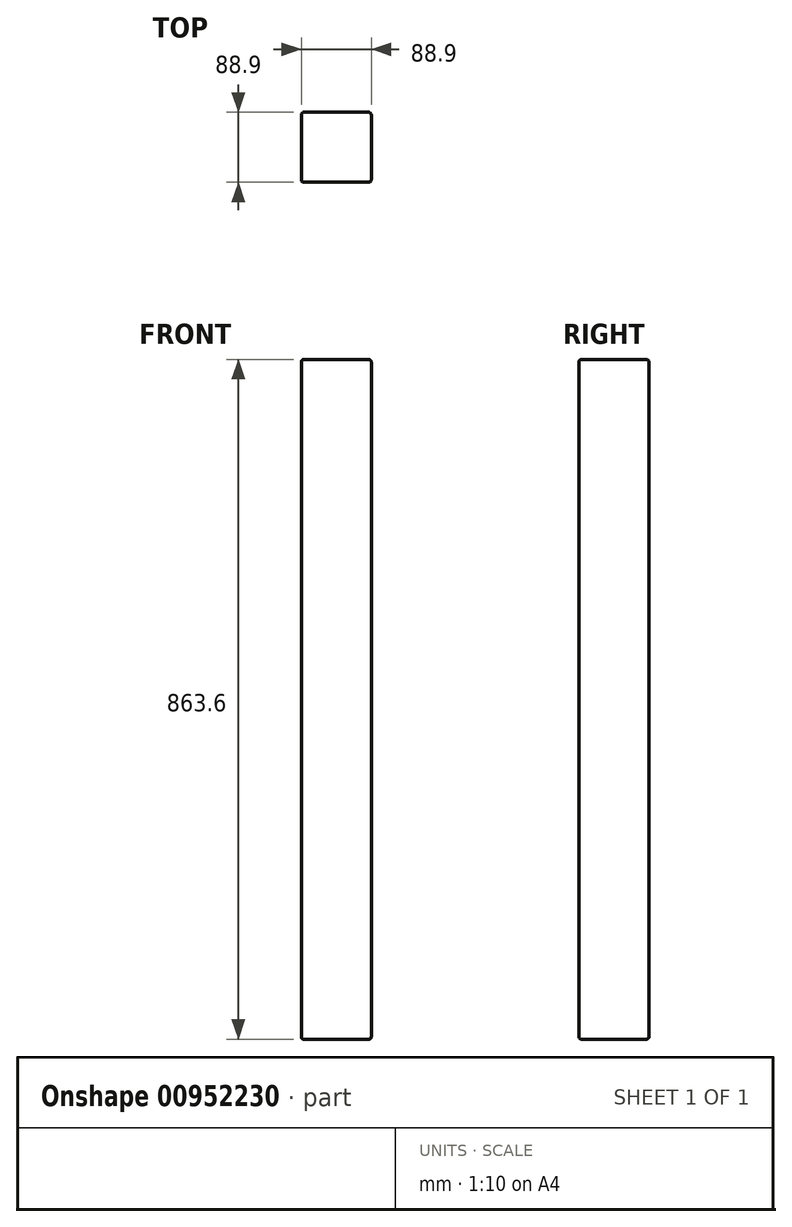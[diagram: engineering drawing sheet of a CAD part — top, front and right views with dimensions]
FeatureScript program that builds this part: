
annotation { "Feature Type Name" : "Feature", "Feature Type Description" : "" }
export const myFeature = defineFeature(function(context is Context, id is Id, definition is map)
    precondition{}
    {
        {
            var Q0;
            Q0=qCreatedBy(makeId("Front.planeOp"),FACE);
            var sketch = newSketch(context, id + "F0", { "sketchPlane" : qUnion([Q0])});
            skLineSegment(sketch, "E0.bottom", {"start": v(88.9, 0) * mm, "end": v(0, 0) * mm});
            skLineSegment(sketch, "E0.top", {"start": v(88.9, -863.6) * mm, "end": v(0, -863.6) * mm});
            skLineSegment(sketch, "E0.left", {"start": v(88.9, 0) * mm, "end": v(88.9, -863.6) * mm});
            skLineSegment(sketch, "E0.right", {"start": v(0, 0) * mm, "end": v(0, -863.6) * mm});
            skSolve(sketch);
        }
        {
            var Q0;
            Q0=makeQuery(id+"F0.imprint","IMPRINT",FACE,{"disambiguationData":[TD([[makeQuery(id+"F0.imprint","IMPRINT",EDGE,{"derivedFrom":sQuery(id+"F0.wireOp",EDGE,"E0.bottom")}),1.0]])]});
            extrude(context, id + "F1", {"entities" : qUnion([Q0]), "depth" : 88.9 * mm, "offsetDistance" : 25.4 * mm});
        }
        {
            var Q0;
            Q0=makeQuery(id+"F1.opExtrude","CAP_EDGE",EDGE,{"disambiguationData":[OSD([sQuery(id+"F0.wireOp",EDGE,"E0.left")])],"isStart":false});
            var Q1;
            Q1=makeQuery(id+"F1.opExtrude","CAP_EDGE",EDGE,{"disambiguationData":[OSD([sQuery(id+"F0.wireOp",EDGE,"E0.left")])],"isStart":true});
            var Q2;
            Q2=makeQuery(id+"F1.opExtrude","CAP_EDGE",EDGE,{"disambiguationData":[OSD([sQuery(id+"F0.wireOp",EDGE,"E0.right")])],"isStart":false});
            var Q3;
            Q3=makeQuery(id+"F1.opExtrude","SWEPT_EDGE",EDGE,{"disambiguationData":[OSD([sQuery(id+"F0.wireOp",EDGE,"E0.bottom"),sQuery(id+"F0.wireOp",EDGE,"E0.left")])]});
            var Q4;
            Q4=makeQuery(id+"F1.opExtrude","CAP_EDGE",EDGE,{"disambiguationData":[OSD([sQuery(id+"F0.wireOp",EDGE,"E0.bottom")])],"isStart":true});
            var Q5;
            Q5=makeQuery(id+"F1.opExtrude","SWEPT_EDGE",EDGE,{"disambiguationData":[OSD([sQuery(id+"F0.wireOp",EDGE,"E0.bottom"),sQuery(id+"F0.wireOp",EDGE,"E0.right")])]});
            var Q6;
            Q6=makeQuery(id+"F1.opExtrude","CAP_EDGE",EDGE,{"disambiguationData":[OSD([sQuery(id+"F0.wireOp",EDGE,"E0.bottom")])],"isStart":false});
            var Q7;
            Q7=makeQuery(id+"F1.opExtrude","CAP_EDGE",EDGE,{"disambiguationData":[OSD([sQuery(id+"F0.wireOp",EDGE,"E0.right")])],"isStart":true});
            var Q8;
            Q8=makeQuery(id+"F1.opExtrude","CAP_EDGE",EDGE,{"disambiguationData":[OSD([sQuery(id+"F0.wireOp",EDGE,"E0.top")])],"isStart":true});
            var Q9;
            Q9=makeQuery(id+"F1.opExtrude","SWEPT_EDGE",EDGE,{"disambiguationData":[OSD([sQuery(id+"F0.wireOp",EDGE,"E0.top"),sQuery(id+"F0.wireOp",EDGE,"E0.right")])]});
            var Q10;
            Q10=makeQuery(id+"F1.opExtrude","SWEPT_EDGE",EDGE,{"disambiguationData":[OSD([sQuery(id+"F0.wireOp",EDGE,"E0.top"),sQuery(id+"F0.wireOp",EDGE,"E0.left")])]});
            var Q11;
            Q11=makeQuery(id+"F1.opExtrude","CAP_EDGE",EDGE,{"disambiguationData":[OSD([sQuery(id+"F0.wireOp",EDGE,"E0.top")])],"isStart":false});
            fillet(context, id + "F2", {"entities" : qUnion([Q0, Q1, Q2, Q3, Q4, Q5, Q6, Q7, Q8, Q9, Q10, Q11]), "radius" : 3.17 * mm, "tangentPropagation" : true, "allowEdgeOverflow" : false});
        }
    });
